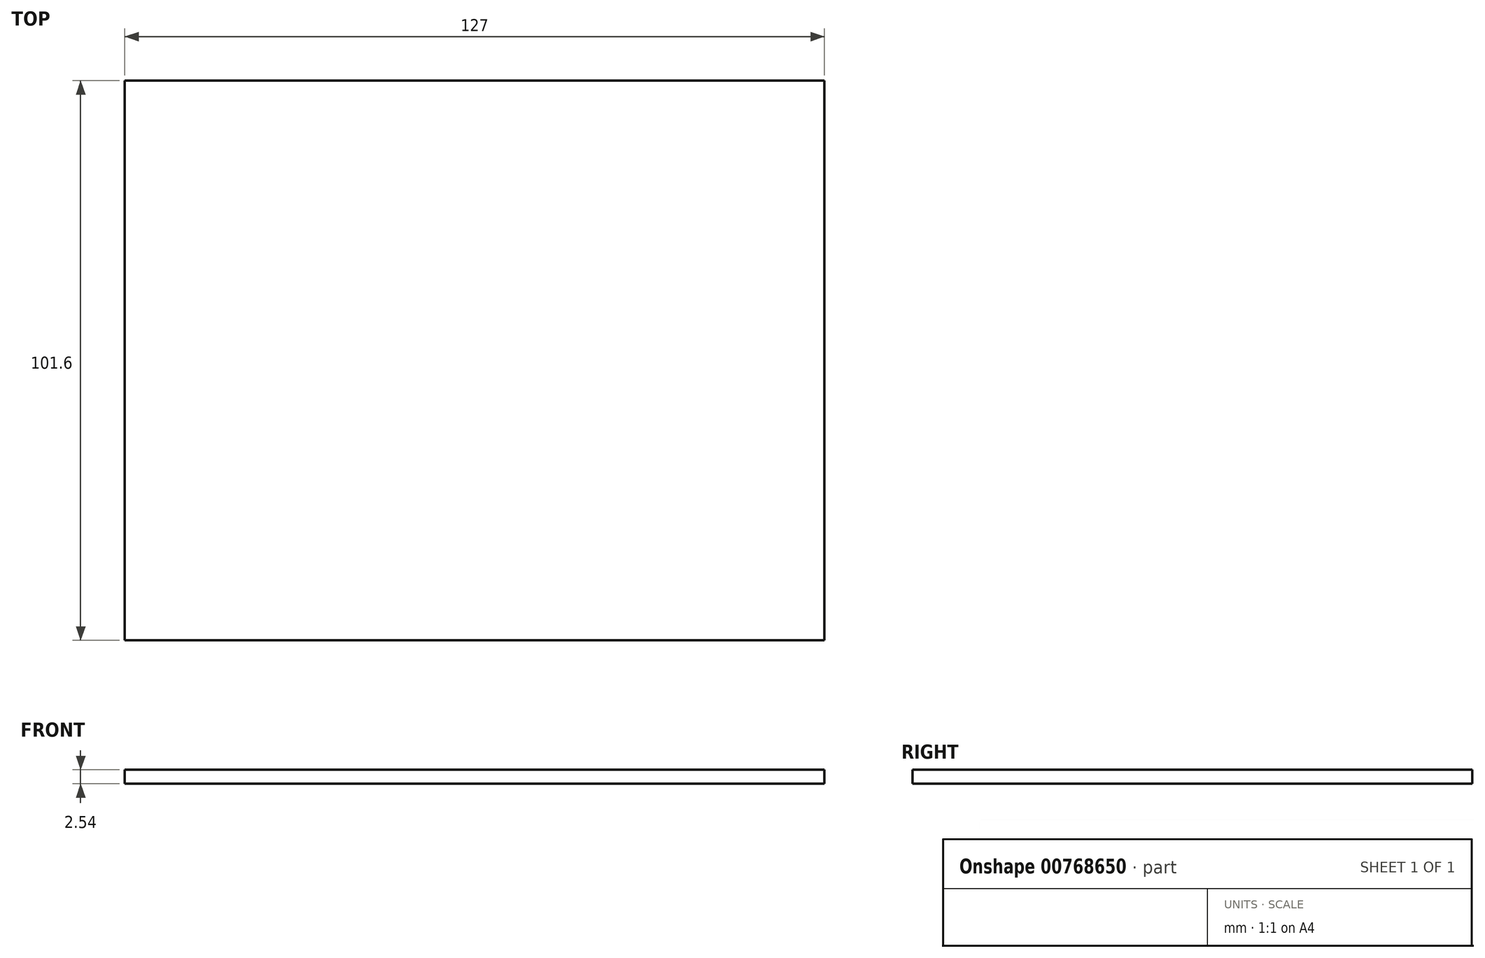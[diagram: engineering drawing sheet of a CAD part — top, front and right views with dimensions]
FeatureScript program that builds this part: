
annotation { "Feature Type Name" : "Feature", "Feature Type Description" : "" }
export const myFeature = defineFeature(function(context is Context, id is Id, definition is map)
    precondition{}
    {
        {
            var Q0;
            Q0=qCreatedBy(makeId("Top.planeOp"),FACE);
            var sketch = newSketch(context, id + "F0", { "sketchPlane" : qUnion([Q0])});
            skLineSegment(sketch, "E0", {"start": v(-76.34, 55.33) * mm, "end": v(-76.34, -46.27) * mm});
            skLineSegment(sketch, "E1", {"start": v(50.66, -46.27) * mm, "end": v(50.66, 55.33) * mm});
            skLineSegment(sketch, "E2", {"start": v(50.66, 55.33) * mm, "end": v(-76.34, 55.33) * mm});
            skLineSegment(sketch, "E3", {"start": v(-76.34, -46.27) * mm, "end": v(50.66, -46.27) * mm});
            skSolve(sketch);
        }
        {
            var Q0;
            Q0=makeQuery(id+"F0.imprint","IMPRINT",FACE,{"disambiguationData":[TD([[makeQuery(id+"F0.imprint","IMPRINT",EDGE,{"derivedFrom":sQuery(id+"F0.wireOp",EDGE,"E0")}),1.0]])]});
            extrude(context, id + "F1", {"entities" : qUnion([Q0]), "depth" : 2.54 * mm, "offsetDistance" : 25.4 * mm});
        }
    });
